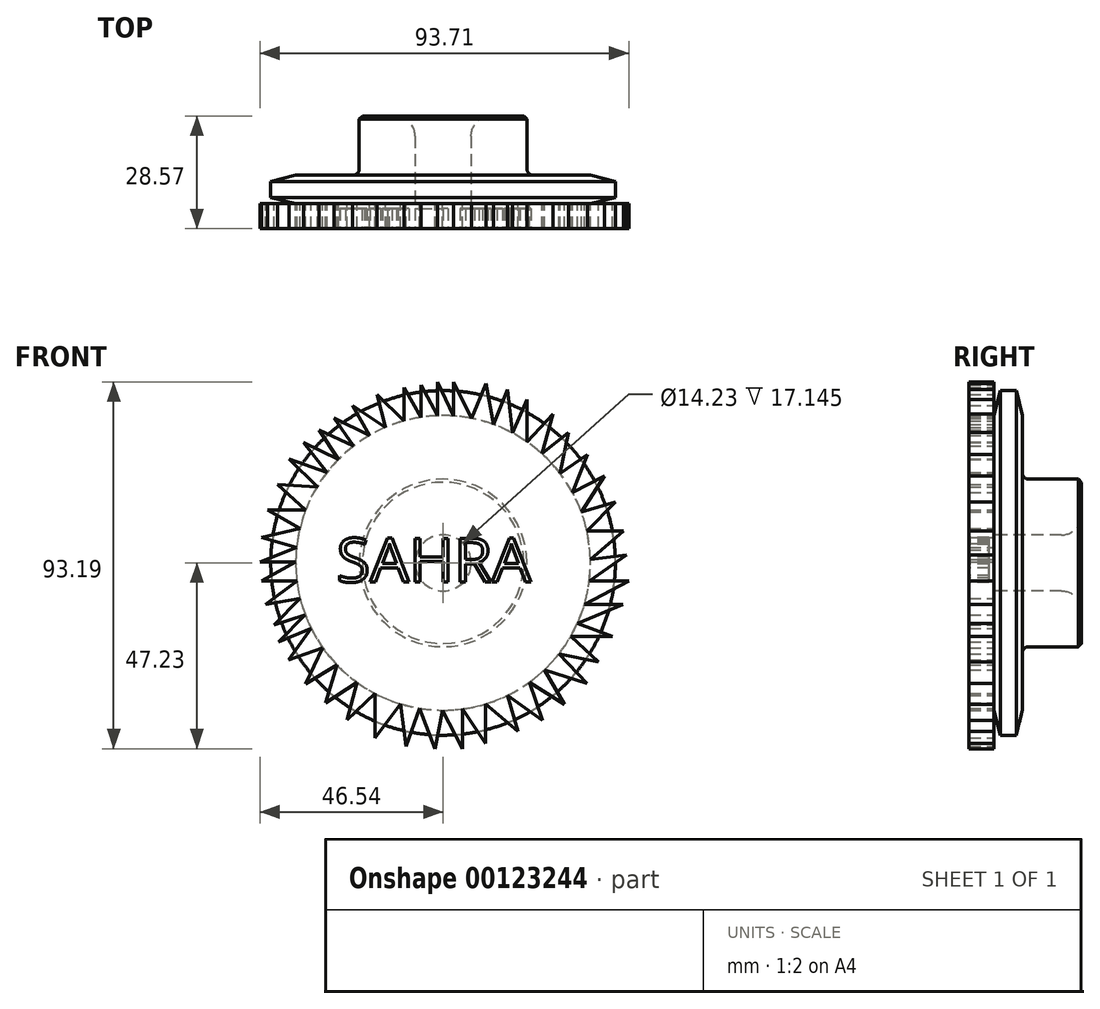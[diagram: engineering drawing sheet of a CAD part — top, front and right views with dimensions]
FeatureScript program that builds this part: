
annotation { "Feature Type Name" : "Feature", "Feature Type Description" : "" }
export const myFeature = defineFeature(function(context is Context, id is Id, definition is map)
    precondition{}
    {
        {
            var Q0;
            Q0=qCreatedBy(makeId("Right.planeOp"),FACE);
            var sketch = newSketch(context, id + "F0", { "sketchPlane" : qUnion([Q0])});
            skLineSegment(sketch, "E0", {"start": v(0, 0) * mm, "end": v(36.39, 0) * mm, "construction": true});
            skLineSegment(sketch, "E1.bottom", {"start": v(-7.21, 47.11) * mm, "end": v(0, 47.11) * mm});
            skLineSegment(sketch, "E1.top", {"start": v(-7.21, 8.76) * mm, "end": v(0, 8.76) * mm, "construction": true});
            skLineSegment(sketch, "E1.left", {"start": v(-7.21, 47.11) * mm, "end": v(-7.21, 8.76) * mm, "construction": true});
            skLineSegment(sketch, "E1.right", {"start": v(0, 47.11) * mm, "end": v(0, 8.76) * mm});
            skLineSegment(sketch, "E2.bottom", {"start": v(-7.21, 8.76) * mm, "end": v(15.01, 8.76) * mm});
            skLineSegment(sketch, "E2.top", {"start": v(-7.21, 29.5) * mm, "end": v(15.01, 29.5) * mm});
            skLineSegment(sketch, "E2.left", {"start": v(-7.21, 8.76) * mm, "end": v(-7.21, 29.5) * mm, "construction": true});
            skLineSegment(sketch, "E2.right", {"start": v(15.01, 8.76) * mm, "end": v(15.01, 29.5) * mm});
            skLineSegment(sketch, "E3.bottom", {"start": v(-9.41, -7.11) * mm, "end": v(-2.2, -7.11) * mm, "construction": true});
            skLineSegment(sketch, "E3.top", {"start": v(-9.41, -43.78) * mm, "end": v(-2.2, -43.78) * mm});
            skLineSegment(sketch, "E3.left", {"start": v(-9.41, -7.11) * mm, "end": v(-9.41, -43.78) * mm});
            skLineSegment(sketch, "E3.right", {"start": v(-2.2, -7.11) * mm, "end": v(-2.2, -43.78) * mm});
            skLineSegment(sketch, "E4.bottom", {"start": v(-9.41, -7.11) * mm, "end": v(12.81, -7.11) * mm});
            skLineSegment(sketch, "E4.top", {"start": v(-9.41, -21.3) * mm, "end": v(12.81, -21.3) * mm});
            skLineSegment(sketch, "E4.left", {"start": v(-9.41, -7.11) * mm, "end": v(-9.41, -21.3) * mm, "construction": true});
            skLineSegment(sketch, "E4.right", {"start": v(12.81, -7.11) * mm, "end": v(12.81, -21.3) * mm});
            skSolve(sketch);
        }
        {
            var Q0;
            {var subQ5=sQuery(id+"F0.wireOp",EDGE,"E4.right");Q0=makeQuery(id+"F0.imprint","IMPRINT",FACE,{"disambiguationData":[TD([[makeQuery(id+"F0.imprint","IMPRINT",EDGE,{"derivedFrom":subQ5}),-1.0]])]});}
            var Q1;
            {var subQ0=sQuery(id+"F0.wireOp",EDGE,"E4.bottom");var subQ1=sQuery(id+"F0.wireOp",EDGE,"E3.left");var subQ2=makeQuery(id+"F0.imprint","INTERSECT",VERTEX,{"derivedFrom":[subQ1,subQ0]});Q1=makeQuery(id+"F0.imprint","IMPRINT",FACE,{"disambiguationData":[TD([[makeQuery(id+"F0.imprint","IMPRINT",EDGE,{"disambiguationData":[TD([[subQ2,-1.0]])],"derivedFrom":subQ1}),1.0]])]});}
            var Q2;
            {var subQ0=sQuery(id+"F0.wireOp",EDGE,"E3.top");Q2=makeQuery(id+"F0.imprint","IMPRINT",FACE,{"disambiguationData":[TD([[makeQuery(id+"F0.imprint","IMPRINT",EDGE,{"derivedFrom":subQ0}),1.0]])]});}
            var Q3;
            Q3=sQuery(id+"F0.wireOp",EDGE,"E0");
            revolve(context, id + "F1", {"entities" : qUnion([Q0, Q1, Q2]), "axis" : qUnion([Q3]), "revolveType" : RevolveType.FULL});
        }
        {
            var Q0;
            Q0=makeQuery(id+"F1.opRevolve","SWEPT_EDGE",EDGE,{"disambiguationData":[OSD([sQuery(id+"F0.wireOp",EDGE,"E3.right"),sQuery(id+"F0.wireOp",EDGE,"E4.top")])]});
            fillet(context, id + "F2", {"entities" : qUnion([Q0]), "radius" : 1.59 * mm, "tangentPropagation" : true, "allowEdgeOverflow" : false});
        }
        {
            var Q0;
            Q0=makeQuery(id+"F1.opRevolve","SWEPT_EDGE",EDGE,{"disambiguationData":[OSD([sQuery(id+"F0.wireOp",EDGE,"E4.top"),sQuery(id+"F0.wireOp",EDGE,"E4.right")])]});
            chamfer(context, id + "F3", {"entities" : qUnion([Q0]), "width" : 0.8 * mm, "tangentPropagation" : true});
        }
        {
            var Q0;
            Q0=makeQuery(id+"F1.opRevolve","SWEPT_EDGE",EDGE,{"disambiguationData":[OSD([sQuery(id+"F0.wireOp",EDGE,"E3.top"),sQuery(id+"F0.wireOp",EDGE,"E3.left")])]});
            var Q1;
            Q1=makeQuery(id+"F1.opRevolve","SWEPT_EDGE",EDGE,{"disambiguationData":[OSD([sQuery(id+"F0.wireOp",EDGE,"E3.top"),sQuery(id+"F0.wireOp",EDGE,"E3.right")])]});
            chamfer(context, id + "F4", {"entities" : qUnion([Q0, Q1]), "chamferType" : ChamferType.TWO_OFFSETS, "width1" : 6.35 * mm, "oppositeDirection" : false, "width2" : 1.57 * mm, "tangentPropagation" : true});
        }
        {
            var Q0;
            Q0=makeQuery(id+"F1.opRevolve","SWEPT_FACE",FACE,{"disambiguationData":[OSD([sQuery(id+"F0.wireOp",EDGE,"E3.left")])]});
            var sketch = newSketch(context, id + "F5", { "sketchPlane" : qUnion([Q0])});
            skLineSegment(sketch, "E5", {"start": v(-31.56, 33.8) * mm, "end": v(-26.61, 26.32) * mm});
            skLineSegment(sketch, "E6", {"start": v(-26.61, 26.32) * mm, "end": v(-31.56, 33.8) * mm});
            skLineSegment(sketch, "E7", {"start": v(-31.56, 33.8) * mm, "end": v(-22.7, 29.76) * mm});
            skLineSegment(sketch, "E8", {"start": v(-27.68, 36.86) * mm, "end": v(-22.7, 29.76) * mm});
            skLineSegment(sketch, "E9", {"start": v(-27.68, 36.86) * mm, "end": v(-18.72, 32.41) * mm});
            skLineSegment(sketch, "E10", {"start": v(-18.72, 32.41) * mm, "end": v(-22.98, 39.96) * mm});
            skLineSegment(sketch, "E11", {"start": v(-22.98, 39.96) * mm, "end": v(-14.62, 34.46) * mm});
            skLineSegment(sketch, "E12", {"start": v(-14.62, 34.46) * mm, "end": v(-16.78, 42.8) * mm});
            skLineSegment(sketch, "E13", {"start": v(-16.78, 42.8) * mm, "end": v(-9.93, 36.09) * mm});
            skLineSegment(sketch, "E14", {"start": v(-9.93, 36.09) * mm, "end": v(-9.93, 44.51) * mm});
            skLineSegment(sketch, "E15", {"start": v(-9.93, 44.51) * mm, "end": v(-5.57, 37.01) * mm});
            skLineSegment(sketch, "E16", {"start": v(-5.57, 37.01) * mm, "end": v(-5.57, 45.18) * mm});
            skLineSegment(sketch, "E17", {"start": v(-5.57, 45.18) * mm, "end": v(-1.37, 37.4) * mm});
            skLineSegment(sketch, "E18", {"start": v(-1.37, 37.4) * mm, "end": v(-1.37, 45.96) * mm});
            skLineSegment(sketch, "E19", {"start": v(-1.37, 45.96) * mm, "end": v(2.62, 37.34) * mm});
            skLineSegment(sketch, "E20", {"start": v(2.62, 37.34) * mm, "end": v(2.62, 45.96) * mm});
            skLineSegment(sketch, "E21", {"start": v(2.62, 45.96) * mm, "end": v(7.18, 36.73) * mm});
            skLineSegment(sketch, "E22", {"start": v(32, 19.4) * mm, "end": v(32, 19.4) * mm});
            skLineSegment(sketch, "E23", {"start": v(17.63, 33.02) * mm, "end": v(21.3, 41.48) * mm});
            skLineSegment(sketch, "E24", {"start": v(21.3, 41.48) * mm, "end": v(21.3, 30.78) * mm});
            skLineSegment(sketch, "E25", {"start": v(21.3, 30.78) * mm, "end": v(27.91, 37.8) * mm});
            skLineSegment(sketch, "E26", {"start": v(27.91, 37.8) * mm, "end": v(25.08, 27.78) * mm});
            skLineSegment(sketch, "E27", {"start": v(25.08, 27.78) * mm, "end": v(25.08, 27.78) * mm});
            skLineSegment(sketch, "E28", {"start": v(25.08, 27.78) * mm, "end": v(31.82, 33.17) * mm});
            skLineSegment(sketch, "E29", {"start": v(31.82, 33.17) * mm, "end": v(29.7, 22.78) * mm});
            skLineSegment(sketch, "E30", {"start": v(29.7, 22.78) * mm, "end": v(36.7, 27.6) * mm});
            skLineSegment(sketch, "E31", {"start": v(36.7, 27.6) * mm, "end": v(32.9, 17.84) * mm});
            skLineSegment(sketch, "E32", {"start": v(32.9, 17.84) * mm, "end": v(41.04, 22.14) * mm});
            skLineSegment(sketch, "E33", {"start": v(41.04, 22.14) * mm, "end": v(35.13, 12.91) * mm});
            skLineSegment(sketch, "E34", {"start": v(35.13, 12.91) * mm, "end": v(35.13, 12.91) * mm});
            skLineSegment(sketch, "E35", {"start": v(35.13, 12.91) * mm, "end": v(43.82, 15.51) * mm});
            skLineSegment(sketch, "E36", {"start": v(43.82, 15.51) * mm, "end": v(36.53, 8.14) * mm});
            skLineSegment(sketch, "E37", {"start": v(36.53, 8.14) * mm, "end": v(45.89, 8.14) * mm});
            skLineSegment(sketch, "E38", {"start": v(45.89, 8.14) * mm, "end": v(37.42, 0.9) * mm});
            skLineSegment(sketch, "E39", {"start": v(37.42, 0.9) * mm, "end": v(46.54, 2.03) * mm});
            skLineSegment(sketch, "E40", {"start": v(46.54, 2.03) * mm, "end": v(37.15, -4.53) * mm});
            skLineSegment(sketch, "E41", {"start": v(37.15, -4.53) * mm, "end": v(47.17, -4.53) * mm});
            skLineSegment(sketch, "E42", {"start": v(47.17, -4.53) * mm, "end": v(35.92, -10.54) * mm});
            skLineSegment(sketch, "E43", {"start": v(35.92, -10.54) * mm, "end": v(45.68, -10.54) * mm});
            skLineSegment(sketch, "E44", {"start": v(45.68, -10.54) * mm, "end": v(34.15, -15.32) * mm});
            skLineSegment(sketch, "E45", {"start": v(34.15, -15.32) * mm, "end": v(43.1, -18.68) * mm});
            skLineSegment(sketch, "E46", {"start": v(43.1, -18.68) * mm, "end": v(32.43, -18.68) * mm});
            skLineSegment(sketch, "E47", {"start": v(32.43, -18.68) * mm, "end": v(39.5, -25.17) * mm});
            skLineSegment(sketch, "E48", {"start": v(39.5, -25.17) * mm, "end": v(29.47, -23.08) * mm});
            skLineSegment(sketch, "E49", {"start": v(29.47, -23.08) * mm, "end": v(36.62, -30.6) * mm});
            skLineSegment(sketch, "E50", {"start": v(36.62, -30.6) * mm, "end": v(25.75, -27.16) * mm});
            skLineSegment(sketch, "E51", {"start": v(25.75, -27.16) * mm, "end": v(30.89, -35.89) * mm});
            skLineSegment(sketch, "E52", {"start": v(30.89, -35.89) * mm, "end": v(21.9, -30.35) * mm});
            skLineSegment(sketch, "E53", {"start": v(21.9, -30.35) * mm, "end": v(25.3, -40.06) * mm});
            skLineSegment(sketch, "E54", {"start": v(25.3, -40.06) * mm, "end": v(16.35, -33.67) * mm});
            skLineSegment(sketch, "E55", {"start": v(16.35, -33.67) * mm, "end": v(19.04, -42.87) * mm});
            skLineSegment(sketch, "E56", {"start": v(19.04, -42.87) * mm, "end": v(10.8, -35.84) * mm});
            skLineSegment(sketch, "E57", {"start": v(10.8, -35.84) * mm, "end": v(10.8, -45.87) * mm});
            skLineSegment(sketch, "E58", {"start": v(10.8, -45.87) * mm, "end": v(4.98, -37.1) * mm});
            skLineSegment(sketch, "E59", {"start": v(4.98, -37.1) * mm, "end": v(4.98, -47.23) * mm});
            skLineSegment(sketch, "E60", {"start": v(4.98, -47.23) * mm, "end": v(-0.18, -37.43) * mm});
            skLineSegment(sketch, "E61", {"start": v(-0.18, -37.43) * mm, "end": v(-2.05, -47.22) * mm});
            skLineSegment(sketch, "E62", {"start": v(-2.05, -47.22) * mm, "end": v(-5.97, -36.95) * mm});
            skLineSegment(sketch, "E63", {"start": v(-5.97, -36.95) * mm, "end": v(-9.4, -46.57) * mm});
            skLineSegment(sketch, "E64", {"start": v(-9.4, -46.57) * mm, "end": v(-10.87, -35.82) * mm});
            skLineSegment(sketch, "E65", {"start": v(-10.87, -35.82) * mm, "end": v(-17.25, -44.5) * mm});
            skLineSegment(sketch, "E66", {"start": v(-17.25, -44.5) * mm, "end": v(-17.25, -33.22) * mm});
            skLineSegment(sketch, "E67", {"start": v(-17.25, -33.22) * mm, "end": v(-24.33, -39.89) * mm});
            skLineSegment(sketch, "E68", {"start": v(-24.33, -39.89) * mm, "end": v(-21.84, -30.4) * mm});
            skLineSegment(sketch, "E69", {"start": v(-21.84, -30.4) * mm, "end": v(-29.8, -35.5) * mm});
            skLineSegment(sketch, "E70", {"start": v(-29.8, -35.5) * mm, "end": v(-27, -25.93) * mm});
            skLineSegment(sketch, "E71", {"start": v(-27, -25.93) * mm, "end": v(-34.93, -30.73) * mm});
            skLineSegment(sketch, "E72", {"start": v(-34.93, -30.73) * mm, "end": v(-30.55, -21.62) * mm});
            skLineSegment(sketch, "E73", {"start": v(-30.55, -21.62) * mm, "end": v(-39.23, -24.6) * mm});
            skLineSegment(sketch, "E74", {"start": v(-39.23, -24.6) * mm, "end": v(-33.5, -16.7) * mm});
            skLineSegment(sketch, "E75", {"start": v(-33.5, -16.7) * mm, "end": v(-41.78, -20.12) * mm});
            skLineSegment(sketch, "E76", {"start": v(-41.78, -20.12) * mm, "end": v(-35.01, -13.23) * mm});
            skLineSegment(sketch, "E77", {"start": v(-35.01, -13.23) * mm, "end": v(-42.93, -15.82) * mm});
            skLineSegment(sketch, "E78", {"start": v(-42.93, -15.82) * mm, "end": v(-36.3, -9.08) * mm});
            skLineSegment(sketch, "E79", {"start": v(-36.3, -9.08) * mm, "end": v(-45.12, -10.6) * mm});
            skLineSegment(sketch, "E80", {"start": v(-45.12, -10.6) * mm, "end": v(-37.14, -4.6) * mm});
            skLineSegment(sketch, "E81", {"start": v(-37.14, -4.6) * mm, "end": v(-46.08, -4.6) * mm});
            skLineSegment(sketch, "E82", {"start": v(-46.08, -4.6) * mm, "end": v(-37.43, 0.2) * mm});
            skLineSegment(sketch, "E83", {"start": v(-37.43, 0.2) * mm, "end": v(-46.54, 0.2) * mm});
            skLineSegment(sketch, "E84", {"start": v(-46.54, 0.2) * mm, "end": v(-37.23, 3.88) * mm});
            skLineSegment(sketch, "E85", {"start": v(-37.23, 3.88) * mm, "end": v(-46.17, 6.52) * mm});
            skLineSegment(sketch, "E86", {"start": v(-46.17, 6.52) * mm, "end": v(-36.4, 8.72) * mm});
            skLineSegment(sketch, "E87", {"start": v(-36.4, 8.72) * mm, "end": v(-44.55, 13.48) * mm});
            skLineSegment(sketch, "E88", {"start": v(-44.55, 13.48) * mm, "end": v(-34.92, 13.48) * mm});
            skLineSegment(sketch, "E89", {"start": v(-34.92, 13.48) * mm, "end": v(-41.99, 19.9) * mm});
            skLineSegment(sketch, "E90", {"start": v(-41.99, 19.9) * mm, "end": v(-31.88, 19.33) * mm});
            skLineSegment(sketch, "E91", {"start": v(-31.88, 19.33) * mm, "end": v(-39.14, 26.4) * mm});
            skLineSegment(sketch, "E92", {"start": v(-39.14, 26.4) * mm, "end": v(-29.5, 23.03) * mm});
            skLineSegment(sketch, "E93", {"start": v(-29.5, 23.03) * mm, "end": v(-35.44, 30.57) * mm});
            skLineSegment(sketch, "E94", {"start": v(-35.44, 30.57) * mm, "end": v(-26.61, 26.32) * mm});
            skLineSegment(sketch, "E95", {"start": v(7.18, 36.73) * mm, "end": v(10.96, 45.58) * mm});
            skLineSegment(sketch, "E96", {"start": v(10.96, 45.58) * mm, "end": v(12.79, 35.18) * mm});
            skLineSegment(sketch, "E97", {"start": v(12.79, 35.18) * mm, "end": v(16.38, 44.12) * mm});
            skLineSegment(sketch, "E98", {"start": v(16.38, 44.12) * mm, "end": v(17.63, 33.02) * mm});
            skSolve(sketch);
        }
        {
            var Q0;
            Q0 = qSketchRegion(id + "F5", true);
            extrude(context, id + "F6", {"entities" : qUnion([Q0]), "operationType" : NewBodyOperationType.ADD, "depth" : 6.35 * mm});
        }
        {
            var Q0;
            Q0=makeQuery(id+"F6.opExtrude","CAP_FACE",FACE,{"disambiguationData":[OSD([sQuery(id+"F5.wireOp",EDGE,"E6"),sQuery(id+"F5.wireOp",EDGE,"E7"),sQuery(id+"F5.wireOp",EDGE,"E8"),sQuery(id+"F5.wireOp",EDGE,"E9"),sQuery(id+"F5.wireOp",EDGE,"E10"),sQuery(id+"F5.wireOp",EDGE,"E11"),sQuery(id+"F5.wireOp",EDGE,"E12"),sQuery(id+"F5.wireOp",EDGE,"E13"),sQuery(id+"F5.wireOp",EDGE,"E14"),sQuery(id+"F5.wireOp",EDGE,"E15"),sQuery(id+"F5.wireOp",EDGE,"E16"),sQuery(id+"F5.wireOp",EDGE,"E17"),sQuery(id+"F5.wireOp",EDGE,"E18"),sQuery(id+"F5.wireOp",EDGE,"E19"),sQuery(id+"F5.wireOp",EDGE,"E20"),sQuery(id+"F5.wireOp",EDGE,"E21"),sQuery(id+"F5.wireOp",EDGE,"E23"),sQuery(id+"F5.wireOp",EDGE,"E24"),sQuery(id+"F5.wireOp",EDGE,"E25"),sQuery(id+"F5.wireOp",EDGE,"E26"),sQuery(id+"F5.wireOp",EDGE,"E28"),sQuery(id+"F5.wireOp",EDGE,"E29"),sQuery(id+"F5.wireOp",EDGE,"E30"),sQuery(id+"F5.wireOp",EDGE,"E31"),sQuery(id+"F5.wireOp",EDGE,"E32"),sQuery(id+"F5.wireOp",EDGE,"E33"),sQuery(id+"F5.wireOp",EDGE,"E35"),sQuery(id+"F5.wireOp",EDGE,"E36"),sQuery(id+"F5.wireOp",EDGE,"E37"),sQuery(id+"F5.wireOp",EDGE,"E38"),sQuery(id+"F5.wireOp",EDGE,"E39"),sQuery(id+"F5.wireOp",EDGE,"E40"),sQuery(id+"F5.wireOp",EDGE,"E41"),sQuery(id+"F5.wireOp",EDGE,"E42"),sQuery(id+"F5.wireOp",EDGE,"E43"),sQuery(id+"F5.wireOp",EDGE,"E44"),sQuery(id+"F5.wireOp",EDGE,"E45"),sQuery(id+"F5.wireOp",EDGE,"E46"),sQuery(id+"F5.wireOp",EDGE,"E47"),sQuery(id+"F5.wireOp",EDGE,"E48"),sQuery(id+"F5.wireOp",EDGE,"E49"),sQuery(id+"F5.wireOp",EDGE,"E50"),sQuery(id+"F5.wireOp",EDGE,"E51"),sQuery(id+"F5.wireOp",EDGE,"E52"),sQuery(id+"F5.wireOp",EDGE,"E53"),sQuery(id+"F5.wireOp",EDGE,"E54"),sQuery(id+"F5.wireOp",EDGE,"E55"),sQuery(id+"F5.wireOp",EDGE,"E56"),sQuery(id+"F5.wireOp",EDGE,"E57"),sQuery(id+"F5.wireOp",EDGE,"E58"),sQuery(id+"F5.wireOp",EDGE,"E59"),sQuery(id+"F5.wireOp",EDGE,"E60"),sQuery(id+"F5.wireOp",EDGE,"E61"),sQuery(id+"F5.wireOp",EDGE,"E62"),sQuery(id+"F5.wireOp",EDGE,"E63"),sQuery(id+"F5.wireOp",EDGE,"E64"),sQuery(id+"F5.wireOp",EDGE,"E65"),sQuery(id+"F5.wireOp",EDGE,"E66"),sQuery(id+"F5.wireOp",EDGE,"E67"),sQuery(id+"F5.wireOp",EDGE,"E68"),sQuery(id+"F5.wireOp",EDGE,"E69"),sQuery(id+"F5.wireOp",EDGE,"E70"),sQuery(id+"F5.wireOp",EDGE,"E71"),sQuery(id+"F5.wireOp",EDGE,"E72"),sQuery(id+"F5.wireOp",EDGE,"E73"),sQuery(id+"F5.wireOp",EDGE,"E74"),sQuery(id+"F5.wireOp",EDGE,"E75"),sQuery(id+"F5.wireOp",EDGE,"E76"),sQuery(id+"F5.wireOp",EDGE,"E77"),sQuery(id+"F5.wireOp",EDGE,"E78"),sQuery(id+"F5.wireOp",EDGE,"E79"),sQuery(id+"F5.wireOp",EDGE,"E80"),sQuery(id+"F5.wireOp",EDGE,"E81"),sQuery(id+"F5.wireOp",EDGE,"E82"),sQuery(id+"F5.wireOp",EDGE,"E83"),sQuery(id+"F5.wireOp",EDGE,"E84"),sQuery(id+"F5.wireOp",EDGE,"E85"),sQuery(id+"F5.wireOp",EDGE,"E86"),sQuery(id+"F5.wireOp",EDGE,"E87"),sQuery(id+"F5.wireOp",EDGE,"E88"),sQuery(id+"F5.wireOp",EDGE,"E89"),sQuery(id+"F5.wireOp",EDGE,"E90"),sQuery(id+"F5.wireOp",EDGE,"E91"),sQuery(id+"F5.wireOp",EDGE,"E92"),sQuery(id+"F5.wireOp",EDGE,"E93"),sQuery(id+"F5.wireOp",EDGE,"E94"),sQuery(id+"F5.wireOp",EDGE,"E95"),sQuery(id+"F5.wireOp",EDGE,"E96"),sQuery(id+"F5.wireOp",EDGE,"E97"),sQuery(id+"F5.wireOp",EDGE,"E98")])],"isStart":false});
            var sketch = newSketch(context, id + "F7", { "sketchPlane" : qUnion([Q0])});
            skText(sketch, "E99", { "text": "SAHRA", "fontName": "OpenSans-Regular.ttf"});
            const initialGuessF7  = {"E99": [-0.02706, -0.00484, 1, 0, 0.01121]};
            skSetInitialGuess(sketch, initialGuessF7);
            skSolve(sketch);
        }
        {
            var Q0;
            Q0=makeQuery(id+"F7.imprint","IMPRINT",FACE,{"disambiguationData":[TD([[makeQuery(id+"F7.imprint","IMPRINT",EDGE,{"derivedFrom":sQuery(id+"F7.wireOp",EDGE,"E99.sketch_text.stroke-38")}),-1.0]])]});
            var Q1;
            Q1=makeQuery(id+"F7.imprint","IMPRINT",FACE,{"disambiguationData":[TD([[makeQuery(id+"F7.imprint","IMPRINT",EDGE,{"derivedFrom":sQuery(id+"F7.wireOp",EDGE,"E99.sketch_text.stroke-25")}),-1.0]])]});
            var Q2;
            Q2=makeQuery(id+"F7.imprint","IMPRINT",FACE,{"disambiguationData":[TD([[makeQuery(id+"F7.imprint","IMPRINT",EDGE,{"derivedFrom":sQuery(id+"F7.wireOp",EDGE,"E99.sketch_text.stroke-0")}),-1.0]])]});
            var Q3;
            Q3=makeQuery(id+"F7.imprint","IMPRINT",FACE,{"disambiguationData":[TD([[makeQuery(id+"F7.imprint","IMPRINT",EDGE,{"derivedFrom":sQuery(id+"F7.wireOp",EDGE,"E99.sketch_text.stroke-50")}),-1.0]])]});
            var Q4;
            Q4=makeQuery(id+"F7.imprint","IMPRINT",FACE,{"disambiguationData":[TD([[makeQuery(id+"F7.imprint","IMPRINT",EDGE,{"derivedFrom":sQuery(id+"F7.wireOp",EDGE,"E99.sketch_text.stroke-68")}),-1.0]])]});
            extrude(context, id + "F8", {"entities" : qUnion([Q0, Q1, Q2, Q3, Q4]), "operationType" : NewBodyOperationType.REMOVE, "oppositeDirection" : true, "depth" : 5.08 * mm});
        }
        {
            var Q0;
            Q0=makeQuery(id+"F1.opRevolve","SWEPT_EDGE",EDGE,{"disambiguationData":[OSD([sQuery(id+"F0.wireOp",EDGE,"E4.bottom"),sQuery(id+"F0.wireOp",EDGE,"E4.right")])]});
            fillet(context, id + "F9", {"entities" : qUnion([Q0]), "radius" : 5.08 * mm, "tangentPropagation" : true, "allowEdgeOverflow" : false});
        }
    });
